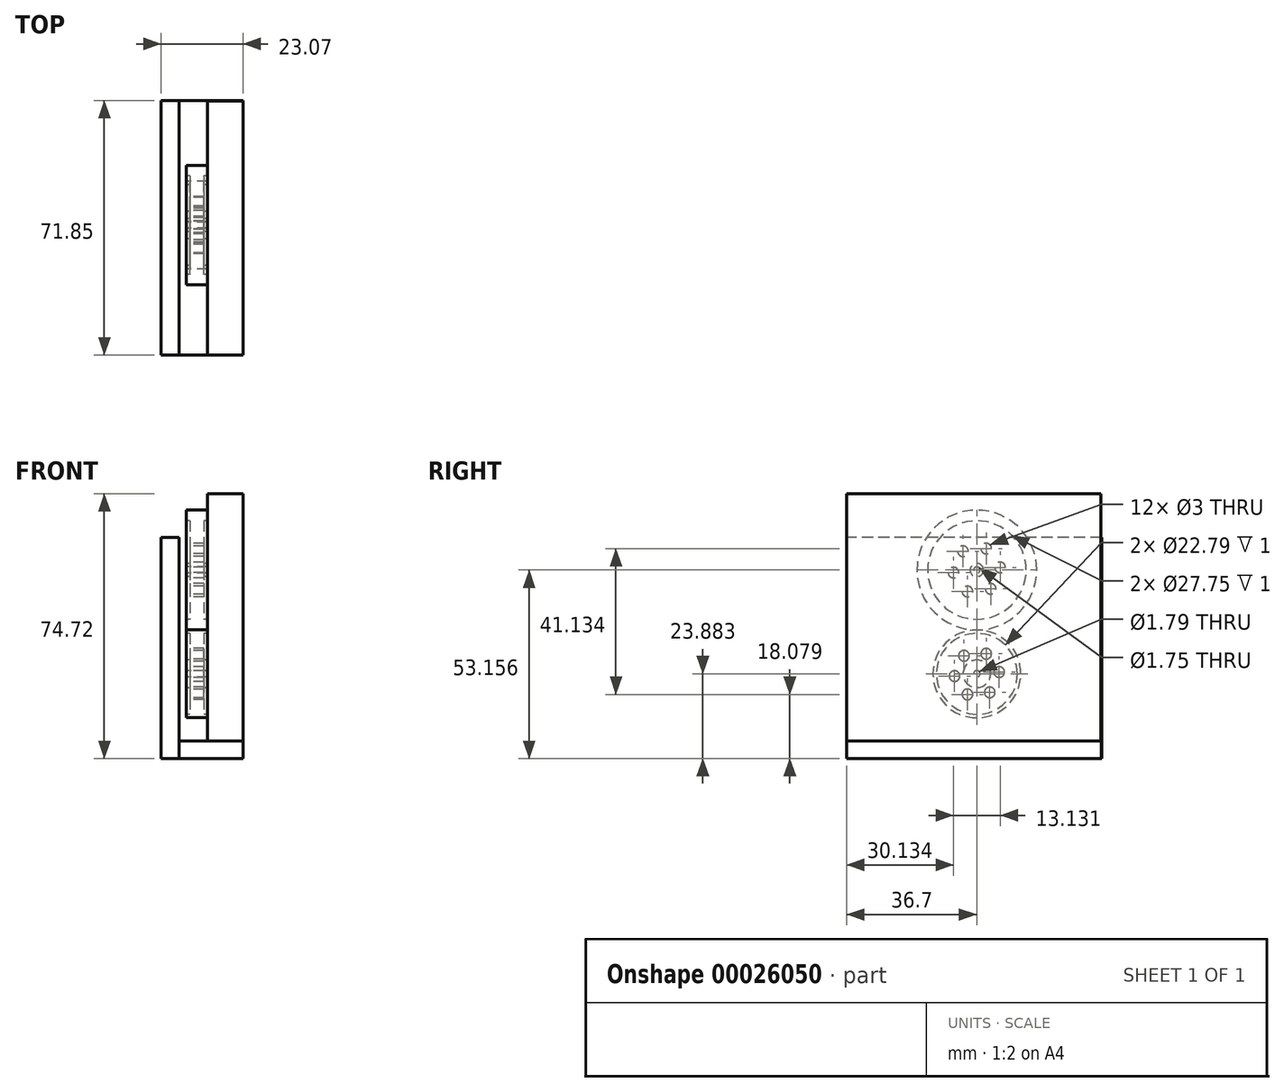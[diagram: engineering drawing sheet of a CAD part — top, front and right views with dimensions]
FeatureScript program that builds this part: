
annotation { "Feature Type Name" : "Feature", "Feature Type Description" : "" }
export const myFeature = defineFeature(function(context is Context, id is Id, definition is map)
    precondition{}
    {
        {
            var Q0;
            Q0=qCreatedBy(makeId("Front.planeOp"),FACE);
            var sketch = newSketch(context, id + "F0", { "sketchPlane" : qUnion([Q0])});
            skLineSegment(sketch, "E0", {"start": v(-6, 3) * mm, "end": v(-5, 3) * mm});
            skLineSegment(sketch, "E1", {"start": v(-5, 3) * mm, "end": v(-5, 15) * mm});
            skLineSegment(sketch, "E2", {"start": v(-5, 15) * mm, "end": v(-6, 15) * mm});
            skLineSegment(sketch, "E3", {"start": v(-6, 15) * mm, "end": v(-6, 16) * mm});
            skLineSegment(sketch, "E4", {"start": v(-6, 16) * mm, "end": v(0, 16) * mm});
            skLineSegment(sketch, "E5", {"start": v(0, 15) * mm, "end": v(0, 16) * mm});
            skLineSegment(sketch, "E6", {"start": v(-1, 15) * mm, "end": v(-1, 3) * mm});
            skLineSegment(sketch, "E7", {"start": v(-1, 3) * mm, "end": v(0, 3) * mm});
            skLineSegment(sketch, "E8", {"start": v(0, 3) * mm, "end": v(0, 0) * mm});
            skLineSegment(sketch, "E9", {"start": v(-1, 15) * mm, "end": v(0, 15) * mm});
            skLineSegment(sketch, "E10", {"start": v(-10.79, 16.88) * mm, "end": v(7.69, 16.88) * mm, "construction": true});
            skLineSegment(sketch, "E11", {"start": v(-6, 0) * mm, "end": v(0, 0) * mm});
            skLineSegment(sketch, "E12", {"start": v(-6, 3) * mm, "end": v(-6, 0) * mm});
            skSolve(sketch);
        }
        {
            var Q0;
            Q0=makeQuery(id+"F0.imprint","IMPRINT",FACE,{"disambiguationData":[TD([[makeQuery(id+"F0.imprint","IMPRINT",EDGE,{"derivedFrom":sQuery(id+"F0.wireOp",EDGE,"E0")}),-1.0]])]});
            var Q1;
            Q1=sQuery(id+"F0.wireOp",EDGE,"E10");
            revolve(context, id + "F1", {"entities" : qUnion([Q0]), "axis" : qUnion([Q1]), "revolveType" : RevolveType.FULL});
        }
        {
            var Q0;
            Q0=qCreatedBy(makeId("Front.planeOp"),FACE);
            var sketch = newSketch(context, id + "F2", { "sketchPlane" : qUnion([Q0])});
            skLineSegment(sketch, "E13", {"start": v(0, 0) * mm, "end": v(0, -1) * mm});
            skLineSegment(sketch, "E14", {"start": v(0, -1) * mm, "end": v(-1, -1) * mm});
            skLineSegment(sketch, "E15", {"start": v(-1, -1) * mm, "end": v(-1, -8.5) * mm});
            skLineSegment(sketch, "E16", {"start": v(-1, -8.5) * mm, "end": v(0, -8.5) * mm});
            skLineSegment(sketch, "E17", {"start": v(0, -8.5) * mm, "end": v(0, -11.5) * mm});
            skLineSegment(sketch, "E18", {"start": v(0, -11.5) * mm, "end": v(-6, -11.5) * mm});
            skLineSegment(sketch, "E19", {"start": v(-6, -11.5) * mm, "end": v(-6, -8.5) * mm});
            skLineSegment(sketch, "E20", {"start": v(-6, -8.5) * mm, "end": v(-5, -8.5) * mm});
            skLineSegment(sketch, "E21", {"start": v(-5, -8.5) * mm, "end": v(-5, -1) * mm});
            skLineSegment(sketch, "E22", {"start": v(-5, -1) * mm, "end": v(-6, -1) * mm});
            skLineSegment(sketch, "E23", {"start": v(-6, -1) * mm, "end": v(-6, 0) * mm});
            skLineSegment(sketch, "E24", {"start": v(-6.58, -12.4) * mm, "end": v(5.43, -12.4) * mm, "construction": true});
            skLineSegment(sketch, "E25", {"start": v(-6, 0) * mm, "end": v(0, 0) * mm});
            skSolve(sketch);
        }
        {
            var Q0;
            Q0 = qSketchRegion(id + "F2", true);
            var Q1;
            Q1=sQuery(id+"F2.wireOp",EDGE,"E24");
            revolve(context, id + "F3", {"entities" : qUnion([Q0]), "axis" : qUnion([Q1]), "revolveType" : RevolveType.FULL});
        }
        {
            var Q0;
            Q0=qCreatedBy(makeId("Right.planeOp"),FACE);
            var sketch = newSketch(context, id + "F4", { "sketchPlane" : qUnion([Q0])});
            skLineSegment(sketch, "E26.bottom", {"start": v(-36.7, 38.44) * mm, "end": v(34.98, 38.44) * mm});
            skLineSegment(sketch, "E26.top", {"start": v(-36.7, -31.28) * mm, "end": v(34.98, -31.28) * mm});
            skLineSegment(sketch, "E26.left", {"start": v(-36.7, 38.44) * mm, "end": v(-36.7, -31.28) * mm});
            skLineSegment(sketch, "E26.right", {"start": v(34.98, 38.44) * mm, "end": v(34.98, -31.28) * mm});
            skSolve(sketch);
        }
        {
            var Q0;
            Q0 = qSketchRegion(id + "F4", true);
            extrude(context, id + "F5", {"entities" : qUnion([Q0]), "depth" : 10 * mm});
        }
        {
            var Q0;
            Q0=makeQuery(id+"F1.opRevolve","SWEPT_FACE",FACE,{"disambiguationData":[OSD([sQuery(id+"F0.wireOp",EDGE,"E1")])]});
            var sketch = newSketch(context, id + "F6", { "sketchPlane" : qUnion([Q0])});
            skCircle(sketch, "E27", {"center": v(-6.57, 17.62) * mm, "radius": 1.5 * mm});
            skCircle(sketch, "E28.1.0", {"center": v(-3.92, 11.56) * mm, "radius": 1.5 * mm});
            skCircle(sketch, "E28.2.0", {"center": v(2.64, 10.82) * mm, "radius": 1.5 * mm});
            skCircle(sketch, "E28.3.0", {"center": v(6.57, 16.14) * mm, "radius": 1.5 * mm});
            skCircle(sketch, "E28.4.0", {"center": v(3.92, 22.2) * mm, "radius": 1.5 * mm});
            skCircle(sketch, "E28.5.0", {"center": v(-2.64, 22.93) * mm, "radius": 1.5 * mm});
            skPoint(sketch, "E28.center", {"position": v(0, 16.88) * mm});
            skCircle(sketch, "E29", {"center": v(-6.3, -11.9) * mm, "radius": 1.5 * mm});
            skCircle(sketch, "E30.1.0", {"center": v(-3.64, -17.63) * mm, "radius": 1.5 * mm});
            skCircle(sketch, "E30.2.0", {"center": v(2.65, -18.2) * mm, "radius": 1.5 * mm});
            skCircle(sketch, "E30.3.0", {"center": v(6.3, -13.04) * mm, "radius": 1.5 * mm});
            skCircle(sketch, "E30.4.0", {"center": v(3.64, -7.3) * mm, "radius": 1.5 * mm});
            skCircle(sketch, "E30.5.0", {"center": v(-2.65, -6.74) * mm, "radius": 1.5 * mm});
            skPoint(sketch, "E30.center", {"position": v(0, -12.47) * mm});
            skSolve(sketch);
        }
        {
            var Q0;
            Q0 = qSketchRegion(id + "F6", true);
            extrude(context, id + "F7", {"entities" : qUnion([Q0]), "operationType" : NewBodyOperationType.REMOVE, "endBound" : BoundingType.UP_TO_NEXT, "oppositeDirection" : true, "depth" : 25 * mm});
        }
        {
            var Q0;
            Q0=makeQuery(id+"F5.opExtrude","SWEPT_FACE",FACE,{"disambiguationData":[OSD([sQuery(id+"F4.wireOp",EDGE,"E26.top")])]});
            var sketch = newSketch(context, id + "F8", { "sketchPlane" : qUnion([Q0])});
            skLineSegment(sketch, "E31.bottom", {"start": v(10, 36.7) * mm, "end": v(-8.07, 36.7) * mm});
            skLineSegment(sketch, "E31.top", {"start": v(10, -35.08) * mm, "end": v(-8.07, -35.08) * mm});
            skLineSegment(sketch, "E31.left", {"start": v(10, 36.7) * mm, "end": v(10, -35.08) * mm});
            skLineSegment(sketch, "E31.right", {"start": v(-8.07, 36.7) * mm, "end": v(-8.07, -35.08) * mm});
            skSolve(sketch);
        }
        {
            var Q0;
            {var subQ5=sQuery(id+"F8.wireOp",EDGE,"E31.top");Q0=makeQuery(id+"F8.imprint","IMPRINT",FACE,{"disambiguationData":[TD([[makeQuery(id+"F8.imprint","IMPRINT",EDGE,{"derivedFrom":subQ5}),-1.0]])]});}
            var Q1;
            {var subQ0=sQuery(id+"F4.wireOp",EDGE,"E26.top");var subQ1=makeQuery(id+"F5.opExtrude","CAP_EDGE",EDGE,{"disambiguationData":[OSD([subQ0])],"isStart":true});Q1=makeQuery(id+"F8.imprint","IMPRINT",FACE,{"disambiguationData":[TD([[makeQuery(id+"F8.imprint","IMPRINT",EDGE,{"derivedFrom":subQ1}),1.0]])]});}
            extrude(context, id + "F9", {"entities" : qUnion([Q0, Q1]), "depth" : 5 * mm});
        }
        {
            var Q0;
            Q0=makeQuery(id+"F9.opExtrude","SWEPT_FACE",FACE,{"disambiguationData":[OSD([sQuery(id+"F8.wireOp",EDGE,"E31.right")])]});
            var sketch = newSketch(context, id + "F10", { "sketchPlane" : qUnion([Q0])});
            skLineSegment(sketch, "E32.bottom", {"start": v(-35.15, 26.1) * mm, "end": v(36.7, 26.1) * mm});
            skLineSegment(sketch, "E32.top", {"start": v(-35.15, -36.28) * mm, "end": v(36.7, -36.28) * mm});
            skLineSegment(sketch, "E32.left", {"start": v(-35.15, 26.1) * mm, "end": v(-35.15, -36.28) * mm});
            skLineSegment(sketch, "E32.right", {"start": v(36.7, 26.1) * mm, "end": v(36.7, -36.28) * mm});
            skSolve(sketch);
        }
        {
            var Q0;
            Q0 = qSketchRegion(id + "F10", true);
            var Q1;
            {var subQ4=sQuery(id+"F10.wireOp",EDGE,"E32.bottom");Q1=makeQuery(id+"F10.imprint","IMPRINT",FACE,{"disambiguationData":[TD([[makeQuery(id+"F10.imprint","IMPRINT",EDGE,{"derivedFrom":subQ4}),-1.0]])]});}
            extrude(context, id + "F11", {"entities" : qUnion([Q0, Q1]), "depth" : 5 * mm});
        }
    });
